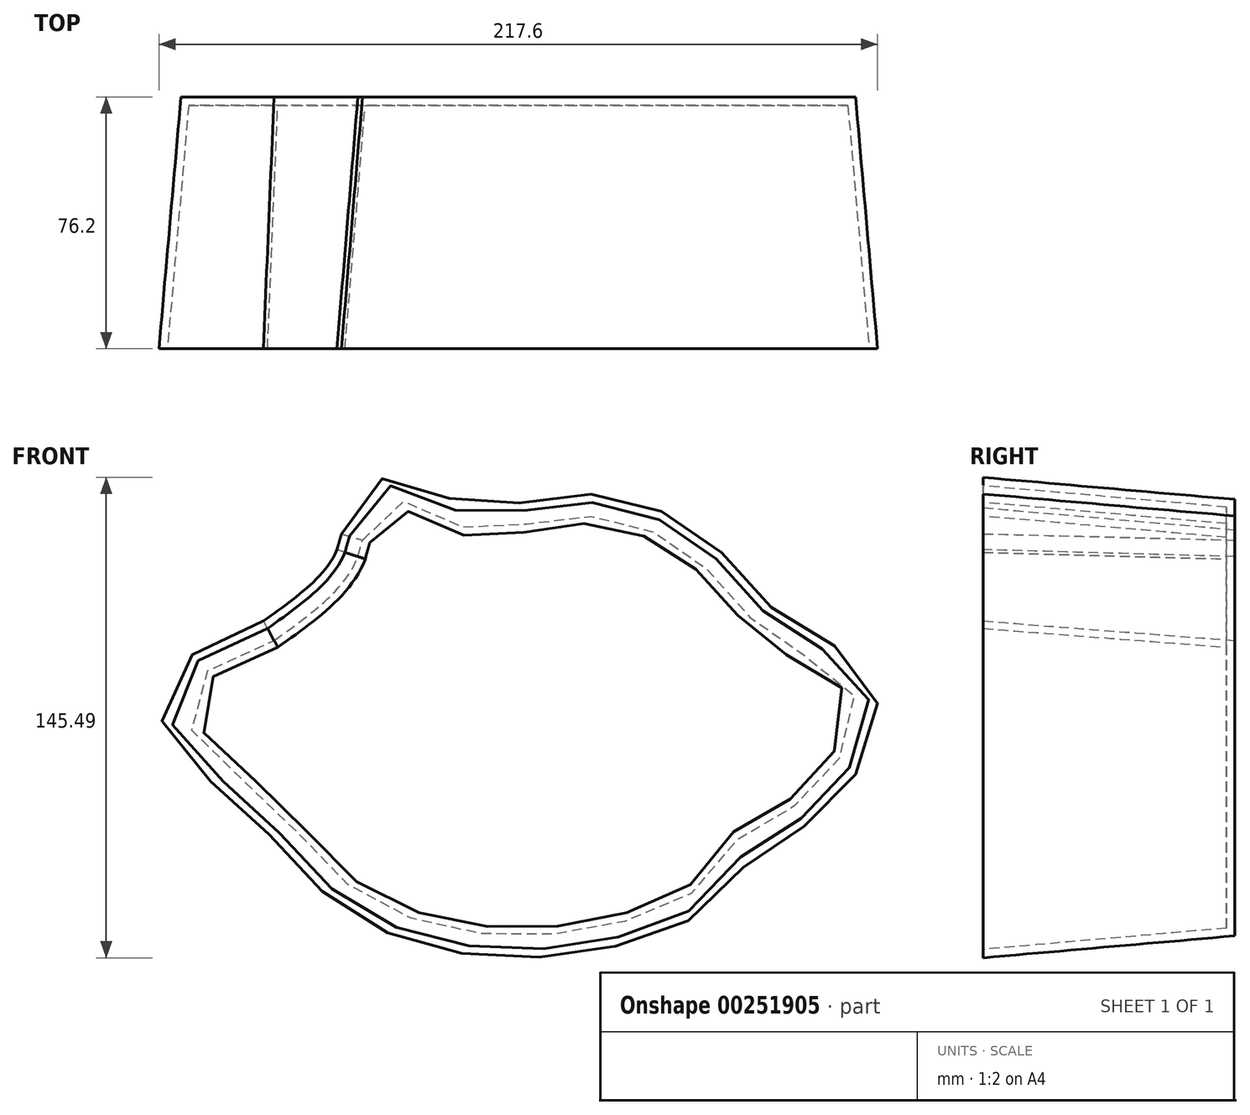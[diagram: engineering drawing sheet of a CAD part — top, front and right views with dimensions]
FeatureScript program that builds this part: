
annotation { "Feature Type Name" : "Feature", "Feature Type Description" : "" }
export const myFeature = defineFeature(function(context is Context, id is Id, definition is map)
    precondition{}
    {
        {
            var Q0;
            Q0=qCreatedBy(makeId("Front.planeOp"),FACE);
            var sketch = newSketch(context, id + "F0", { "sketchPlane" : qUnion([Q0])});
            skPoint(sketch, "E0.visualSharp", {"position": v(-75.6, 51.53) * mm});
            skPoint(sketch, "E1.visualSharp", {"position": v(76.8, 51.53) * mm});
            skPoint(sketch, "E2.visualSharp", {"position": v(-75.6, -50.07) * mm});
            skPoint(sketch, "E3.visualSharp", {"position": v(76.8, -50.07) * mm});
            skFitSpline(sketch, "E4", {"points": [v(-75.6, 26.13) * mm, v(-50.2, 51.53) * mm, v(-44.71, 69.42) * mm, v(-24, 64) * mm, v(0, 65.9) * mm], "startDerivative": vector(107.11, 75.83) * mm, "endDerivative": vector(93.69, 23.98) * mm});
            skFitSpline(sketch, "E5", {"points": [v(-50.2, 51.53) * mm, v(-40.95, 68.71) * mm, v(-17.41, 60.24) * mm, v(15.53, 63.77) * mm, v(51.4, 51.53) * mm, v(76.8, 26.13) * mm, v(100.25, 8.7) * mm, v(84.95, -22.83) * mm, v(76.8, -24.67) * mm, v(62.6, -36.71) * mm, v(51.4, -50.07) * mm, v(0, -63.3) * mm, v(-50.2, -50.07) * mm, v(-75.6, -24.67) * mm, v(-103.78, 6.82) * mm, v(-75.6, 26.13) * mm], "startDerivative": vector(123.6, 453.01) * mm, "endDerivative": vector(597.01, 239.72) * mm});
            skSolve(sketch);
        }
        {
            var Q0;
            Q0 = qSketchRegion(id + "F0", true);
            extrude(context, id + "F1", {"entities" : qUnion([Q0]), "depth" : 76.2 * mm, "hasDraft" : true, "draftAngle" : 5 * degree});
        }
        {
            var Q0;
            Q0=makeQuery(id+"F1.opExtrude","CAP_FACE",FACE,{"disambiguationData":[OSD([sQuery(id+"F0.wireOp",EDGE,"E4"),sQuery(id+"F0.wireOp",EDGE,"E5")])],"isStart":false});
            shell(context, id + "F2", {"entities" : qUnion([Q0]), "thickness" : 2.54 * mm});
        }
    });
